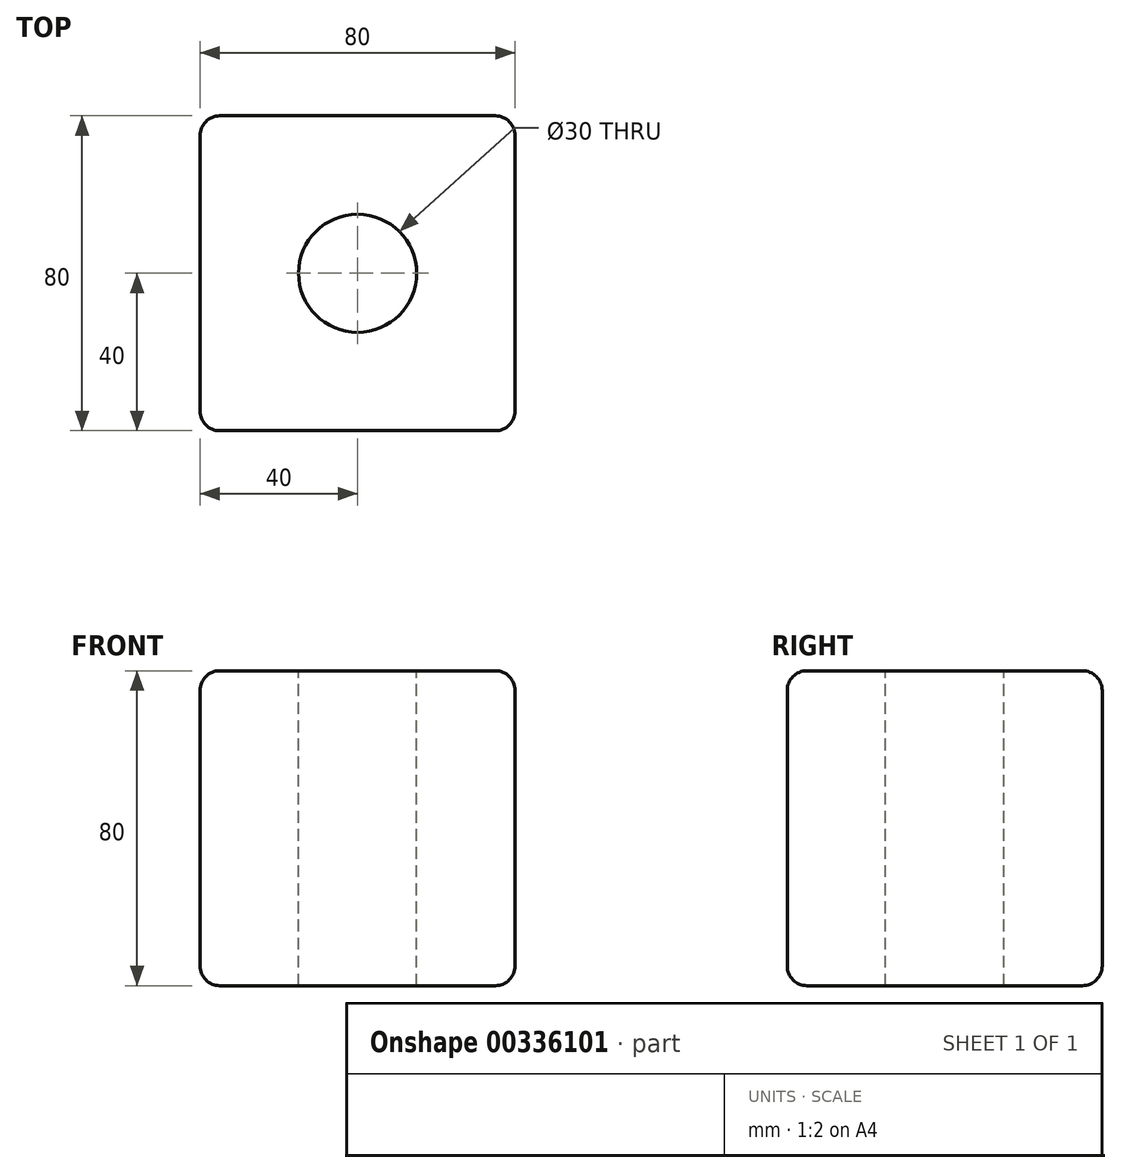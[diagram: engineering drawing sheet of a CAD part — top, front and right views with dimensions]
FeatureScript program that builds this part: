
annotation { "Feature Type Name" : "Feature", "Feature Type Description" : "" }
export const myFeature = defineFeature(function(context is Context, id is Id, definition is map)
    precondition{}
    {
        {
            var Q0;
            Q0=qCreatedBy(makeId("Top.planeOp"),FACE);
            var sketch = newSketch(context, id + "F0", { "sketchPlane" : qUnion([Q0])});
            skLineSegment(sketch, "E0.bottom", {"start": v(-40, -40) * mm, "end": v(40, -40) * mm});
            skLineSegment(sketch, "E0.top", {"start": v(-40, 40) * mm, "end": v(40, 40) * mm});
            skLineSegment(sketch, "E0.left", {"start": v(-40, -40) * mm, "end": v(-40, 40) * mm});
            skLineSegment(sketch, "E0.right", {"start": v(40, -40) * mm, "end": v(40, 40) * mm});
            skPoint(sketch, "E0.middle", {"position": v(0, 0) * mm});
            skSolve(sketch);
        }
        {
            var Q0;
            Q0=makeQuery(id+"F0.imprint","IMPRINT",FACE,{"disambiguationData":[TD([[makeQuery(id+"F0.imprint","IMPRINT",EDGE,{"derivedFrom":sQuery(id+"F0.wireOp",EDGE,"E0.bottom")}),1.0]])]});
            extrude(context, id + "F1", {"entities" : qUnion([Q0]), "endBound" : BoundingType.SYMMETRIC, "depth" : 80 * mm});
        }
        {
            var Q0;
            Q0=makeQuery(id+"F1.opExtrude","SWEPT_FACE",FACE,{"disambiguationData":[OSD([sQuery(id+"F0.wireOp",EDGE,"E0.bottom")])]});
            var Q1;
            Q1=makeQuery(id+"F1.opExtrude","CAP_FACE",FACE,{"disambiguationData":[OSD([sQuery(id+"F0.wireOp",EDGE,"E0.bottom"),sQuery(id+"F0.wireOp",EDGE,"E0.top"),sQuery(id+"F0.wireOp",EDGE,"E0.left"),sQuery(id+"F0.wireOp",EDGE,"E0.right")])],"isStart":false});
            var Q2;
            Q2=makeQuery(id+"F1.opExtrude","SWEPT_FACE",FACE,{"disambiguationData":[OSD([sQuery(id+"F0.wireOp",EDGE,"E0.left")])]});
            var Q3;
            Q3=makeQuery(id+"F1.opExtrude","CAP_FACE",FACE,{"disambiguationData":[OSD([sQuery(id+"F0.wireOp",EDGE,"E0.bottom"),sQuery(id+"F0.wireOp",EDGE,"E0.top"),sQuery(id+"F0.wireOp",EDGE,"E0.left"),sQuery(id+"F0.wireOp",EDGE,"E0.right")])],"isStart":true});
            var Q4;
            Q4=makeQuery(id+"F1.opExtrude","SWEPT_FACE",FACE,{"disambiguationData":[OSD([sQuery(id+"F0.wireOp",EDGE,"E0.top")])]});
            var Q5;
            Q5=makeQuery(id+"F1.opExtrude","SWEPT_FACE",FACE,{"disambiguationData":[OSD([sQuery(id+"F0.wireOp",EDGE,"E0.right")])]});
            fillet(context, id + "F2", {"entities" : qUnion([Q0, Q1, Q2, Q3, Q4, Q5]), "radius" : 5 * mm, "tangentPropagation" : true, "allowEdgeOverflow" : false});
        }
        {
            var Q0;
            Q0=sQuery(id+"F0.wireOp",VERTEX,"E0.middle");
            var Q1;
            Q1=makeQuery(id+"F1.opExtrude","SWEPT_BODY",BODY,{"disambiguationData":[OSD([sQuery(id+"F0.wireOp",EDGE,"E0.bottom"),sQuery(id+"F0.wireOp",EDGE,"E0.top"),sQuery(id+"F0.wireOp",EDGE,"E0.left"),sQuery(id+"F0.wireOp",EDGE,"E0.right")])]});
            hole(context, id + "F3", {"style" : HoleStyle.SIMPLE, "endStyle" : HoleEndStyle.THROUGH, "holeDiameter" : 30 * mm, "isTappedThrough" : true, "tappedDepth" : 12 * mm, "tapClearance" : 3, "locations" : qUnion([Q0]), "scope" : qUnion([Q1])});
        }
        {
            var Q0;
            Q0=sQuery(id+"F0.wireOp",VERTEX,"E0.middle");
            var Q1;
            Q1=makeQuery(id+"F1.opExtrude","SWEPT_BODY",BODY,{"disambiguationData":[OSD([sQuery(id+"F0.wireOp",EDGE,"E0.bottom"),sQuery(id+"F0.wireOp",EDGE,"E0.top"),sQuery(id+"F0.wireOp",EDGE,"E0.left"),sQuery(id+"F0.wireOp",EDGE,"E0.right")])]});
            hole(context, id + "F4", {"style" : HoleStyle.SIMPLE, "endStyle" : HoleEndStyle.THROUGH, "oppositeDirection" : true, "holeDiameter" : 30 * mm, "isTappedThrough" : true, "tappedDepth" : 12 * mm, "tapClearance" : 3, "locations" : qUnion([Q0]), "scope" : qUnion([Q1])});
        }
    });
